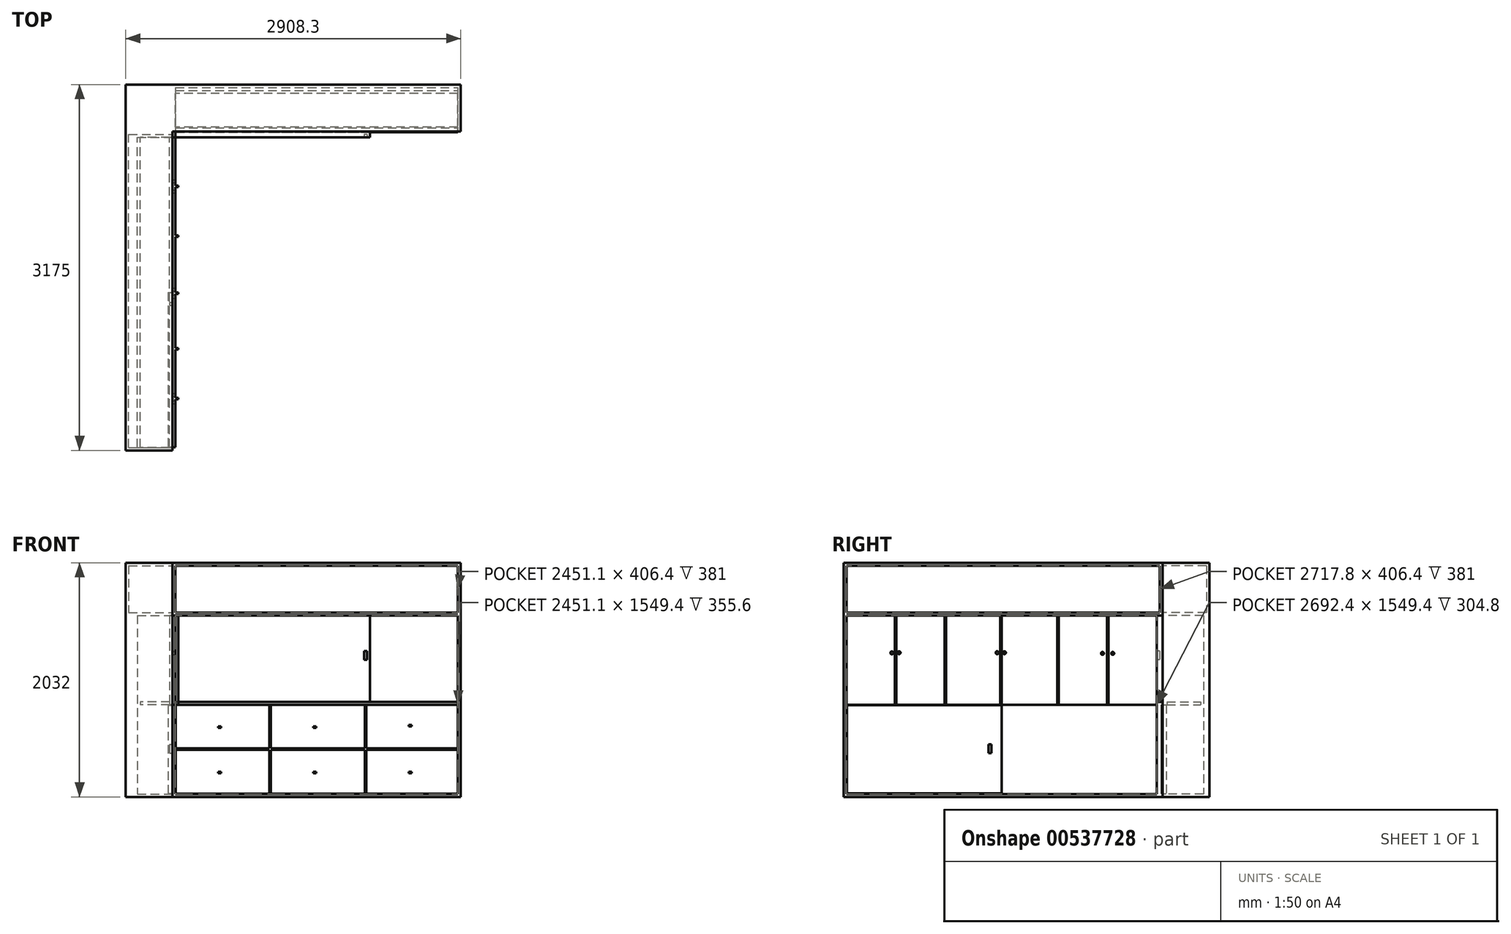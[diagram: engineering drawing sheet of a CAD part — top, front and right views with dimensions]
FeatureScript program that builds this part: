
annotation { "Feature Type Name" : "Feature", "Feature Type Description" : "" }
export const myFeature = defineFeature(function(context is Context, id is Id, definition is map)
    precondition{}
    {
        {
            var Q0;
            Q0=qCreatedBy(makeId("Top.planeOp"),FACE);
            var sketch = newSketch(context, id + "F0", { "sketchPlane" : qUnion([Q0])});
            skLineSegment(sketch, "E0", {"start": v(0, 0) * mm, "end": v(0, 3175) * mm});
            skLineSegment(sketch, "E1", {"start": v(0, 3175) * mm, "end": v(2908.3, 3175) * mm});
            skLineSegment(sketch, "E2", {"start": v(2908.3, 3175) * mm, "end": v(2908.3, 2768.6) * mm});
            skLineSegment(sketch, "E3", {"start": v(0, 0) * mm, "end": v(406.4, 0) * mm});
            skLineSegment(sketch, "E4", {"start": v(406.4, 0) * mm, "end": v(406.4, 2768.6) * mm});
            skLineSegment(sketch, "E5", {"start": v(406.4, 2768.6) * mm, "end": v(2908.3, 2768.6) * mm});
            skSolve(sketch);
        }
        {
            var Q0;
            Q0 = qSketchRegion(id + "F0", true);
            extrude(context, id + "F1", {"entities" : qUnion([Q0]), "depth" : 2032 * mm, "offsetDistance" : 25.4 * mm});
        }
        {
            var Q0;
            Q0=makeQuery(id+"F1.opExtrude","SWEPT_FACE",FACE,{"disambiguationData":[OSD([sQuery(id+"F0.wireOp",EDGE,"E4")])]});
            cPlane(context, id + "F2", {"entities" : qUnion([Q0]), "cplaneType" : CPlaneType.OFFSET, "offset" : 25.4 * mm, "width" : 152.4 * mm, "height" : 152.4 * mm});
        }
        {
            var Q0;
            Q0=makeQuery(id+"F1.opExtrude","SWEPT_FACE",FACE,{"disambiguationData":[OSD([sQuery(id+"F0.wireOp",EDGE,"E4")])]});
            var sketch = newSketch(context, id + "F3", { "sketchPlane" : qUnion([Q0])});
            skLineSegment(sketch, "E6.bottom", {"start": v(25.4, 2006.6) * mm, "end": v(2743.2, 2006.6) * mm});
            skLineSegment(sketch, "E6.top", {"start": v(25.4, 1600.2) * mm, "end": v(2743.2, 1600.2) * mm});
            skLineSegment(sketch, "E6.left", {"start": v(25.4, 2006.6) * mm, "end": v(25.4, 1600.2) * mm});
            skLineSegment(sketch, "E6.right", {"start": v(2743.2, 2006.6) * mm, "end": v(2743.2, 1600.2) * mm});
            skSolve(sketch);
        }
        {
            var Q0;
            Q0=makeQuery(id+"F3.imprint","IMPRINT",FACE,{"disambiguationData":[TD([[makeQuery(id+"F3.imprint","IMPRINT",EDGE,{"derivedFrom":sQuery(id+"F3.wireOp",EDGE,"E6.bottom")}),-1.0]])]});
            extrude(context, id + "F4", {"entities" : qUnion([Q0]), "operationType" : NewBodyOperationType.REMOVE, "oppositeDirection" : true, "depth" : 381 * mm, "offsetDistance" : 25.4 * mm});
        }
        {
            var Q0;
            Q0=qCreatedBy(id+"F2.planeOp",FACE);
            var sketch = newSketch(context, id + "F5", { "sketchPlane" : qUnion([Q0])});
            skLineSegment(sketch, "E7.bottom", {"start": v(25.4, 1574.8) * mm, "end": v(2717.8, 1574.8) * mm});
            skLineSegment(sketch, "E7.top", {"start": v(25.4, 25.4) * mm, "end": v(2717.8, 25.4) * mm});
            skLineSegment(sketch, "E7.left", {"start": v(25.4, 1574.8) * mm, "end": v(25.4, 25.4) * mm});
            skLineSegment(sketch, "E7.right", {"start": v(2717.8, 1574.8) * mm, "end": v(2717.8, 25.4) * mm});
            skSolve(sketch);
        }
        {
            var Q0;
            Q0 = qSketchRegion(id + "F5", true);
            extrude(context, id + "F6", {"entities" : qUnion([Q0]), "operationType" : NewBodyOperationType.REMOVE, "oppositeDirection" : true, "depth" : 330.2 * mm, "offsetDistance" : 25.4 * mm});
        }
        {
            var Q0;
            Q0=makeQuery(id+"F1.opExtrude","SWEPT_FACE",FACE,{"disambiguationData":[OSD([sQuery(id+"F0.wireOp",EDGE,"E5")])]});
            cPlane(context, id + "F7", {"entities" : qUnion([Q0]), "cplaneType" : CPlaneType.OFFSET, "offset" : 25.4 * mm, "width" : 152.4 * mm, "height" : 152.4 * mm});
        }
        {
            var Q0;
            Q0=qCreatedBy(id+"F7.planeOp",FACE);
            var sketch = newSketch(context, id + "F8", { "sketchPlane" : qUnion([Q0])});
            skLineSegment(sketch, "E8.bottom", {"start": v(431.8, 2006.6) * mm, "end": v(2882.9, 2006.6) * mm});
            skLineSegment(sketch, "E8.top", {"start": v(431.8, 1600.2) * mm, "end": v(2882.9, 1600.2) * mm});
            skLineSegment(sketch, "E8.left", {"start": v(431.8, 2006.6) * mm, "end": v(431.8, 1600.2) * mm});
            skLineSegment(sketch, "E8.right", {"start": v(2882.9, 2006.6) * mm, "end": v(2882.9, 1600.2) * mm});
            skSolve(sketch);
        }
        {
            var Q0;
            Q0 = qSketchRegion(id + "F8", true);
            extrude(context, id + "F9", {"entities" : qUnion([Q0]), "operationType" : NewBodyOperationType.REMOVE, "oppositeDirection" : true, "depth" : 406.4 * mm, "offsetDistance" : 25.4 * mm});
        }
        {
            var Q0;
            Q0=makeQuery(id+"F6.boolean.opBoolean","COPY",FACE,{"derivedFrom":makeQuery(id+"F6.opExtrude","CAP_FACE",FACE,{"disambiguationData":[OSD([sQuery(id+"F5.wireOp",EDGE,"E7.bottom"),sQuery(id+"F5.wireOp",EDGE,"E7.top"),sQuery(id+"F5.wireOp",EDGE,"E7.left"),sQuery(id+"F5.wireOp",EDGE,"E7.right")])],"isStart":false})});
            cPlane(context, id + "F10", {"entities" : qUnion([Q0]), "cplaneType" : CPlaneType.OFFSET, "offset" : 25.4 * mm, "width" : 152.4 * mm, "height" : 152.4 * mm});
        }
        {
            var Q0;
            Q0=qCreatedBy(id+"F10.planeOp",FACE);
            var sketch = newSketch(context, id + "F11", { "sketchPlane" : qUnion([Q0])});
            skLineSegment(sketch, "E9.bottom", {"start": v(25.4, 825.5) * mm, "end": v(2717.8, 825.5) * mm});
            skLineSegment(sketch, "E9.top", {"start": v(25.4, 800.1) * mm, "end": v(2717.8, 800.1) * mm});
            skLineSegment(sketch, "E9.left", {"start": v(25.4, 825.5) * mm, "end": v(25.4, 800.1) * mm});
            skLineSegment(sketch, "E9.right", {"start": v(2717.8, 825.5) * mm, "end": v(2717.8, 800.1) * mm});
            skSolve(sketch);
        }
        {
            var Q0;
            Q0=makeQuery(id+"F11.imprint","IMPRINT",FACE,{"disambiguationData":[TD([[makeQuery(id+"F11.imprint","IMPRINT",EDGE,{"derivedFrom":sQuery(id+"F11.wireOp",EDGE,"E9.bottom")}),-1.0]])]});
            extrude(context, id + "F12", {"entities" : qUnion([Q0]), "depth" : 254 * mm, "offsetDistance" : 25.4 * mm});
        }
        {
            var Q0;
            Q0=makeQuery(id+"F12.opExtrude","CAP_FACE",FACE,{"disambiguationData":[OSD([sQuery(id+"F11.wireOp",EDGE,"E9.bottom"),sQuery(id+"F11.wireOp",EDGE,"E9.top"),sQuery(id+"F11.wireOp",EDGE,"E9.left"),sQuery(id+"F11.wireOp",EDGE,"E9.right")])],"isStart":false});
            cPlane(context, id + "F13", {"entities" : qUnion([Q0]), "cplaneType" : CPlaneType.OFFSET, "offset" : 25.4 * mm, "width" : 152.4 * mm, "height" : 152.4 * mm});
        }
        {
            var Q0;
            Q0=qCreatedBy(id+"F13.planeOp",FACE);
            var sketch = newSketch(context, id + "F14", { "sketchPlane" : qUnion([Q0])});
            skLineSegment(sketch, "E10.bottom", {"start": v(1371.6, 795.02) * mm, "end": v(29.21, 795.02) * mm});
            skLineSegment(sketch, "E10.top", {"start": v(1371.6, 29.2) * mm, "end": v(29.21, 29.2) * mm});
            skLineSegment(sketch, "E10.left", {"start": v(1371.6, 795.02) * mm, "end": v(1371.6, 29.2) * mm});
            skLineSegment(sketch, "E10.right", {"start": v(29.21, 795.02) * mm, "end": v(29.21, 29.2) * mm});
            skSolve(sketch);
        }
        {
            var Q0;
            Q0 = qSketchRegion(id + "F14", true);
            extrude(context, id + "F15", {"entities" : qUnion([Q0]), "operationType" : NewBodyOperationType.ADD, "oppositeDirection" : true, "depth" : 38.1 * mm, "offsetDistance" : 25.4 * mm});
        }
        {
            var Q0;
            Q0=makeQuery(id+"F1.opExtrude","SWEPT_FACE",FACE,{"disambiguationData":[OSD([sQuery(id+"F0.wireOp",EDGE,"E5")])]});
            cPlane(context, id + "F16", {"entities" : qUnion([Q0]), "cplaneType" : CPlaneType.OFFSET, "offset" : 25.4 * mm, "width" : 152.4 * mm, "height" : 152.4 * mm});
        }
        {
            var Q0;
            Q0=makeQuery(id+"F1.opExtrude","SWEPT_FACE",FACE,{"disambiguationData":[OSD([sQuery(id+"F0.wireOp",EDGE,"E5")])]});
            var sketch = newSketch(context, id + "F17", { "sketchPlane" : qUnion([Q0])});
            skLineSegment(sketch, "E11.bottom", {"start": v(431.8, 1574.8) * mm, "end": v(2882.9, 1574.8) * mm});
            skLineSegment(sketch, "E11.top", {"start": v(431.8, 25.4) * mm, "end": v(2882.9, 25.4) * mm});
            skLineSegment(sketch, "E11.left", {"start": v(431.8, 1574.8) * mm, "end": v(431.8, 25.4) * mm});
            skLineSegment(sketch, "E11.right", {"start": v(2882.9, 1574.8) * mm, "end": v(2882.9, 25.4) * mm});
            skSolve(sketch);
        }
        {
            var Q0;
            Q0 = qSketchRegion(id + "F17", true);
            extrude(context, id + "F18", {"entities" : qUnion([Q0]), "operationType" : NewBodyOperationType.REMOVE, "oppositeDirection" : true, "depth" : 355.6 * mm, "offsetDistance" : 25.4 * mm});
        }
        {
            var Q0;
            Q0=makeQuery(id+"F18.boolean.opBoolean","COPY",FACE,{"derivedFrom":makeQuery(id+"F18.opExtrude","CAP_FACE",FACE,{"disambiguationData":[OSD([sQuery(id+"F17.wireOp",EDGE,"E11.bottom"),sQuery(id+"F17.wireOp",EDGE,"E11.top"),sQuery(id+"F17.wireOp",EDGE,"E11.left"),sQuery(id+"F17.wireOp",EDGE,"E11.right")])],"isStart":false})});
            cPlane(context, id + "F19", {"entities" : qUnion([Q0]), "cplaneType" : CPlaneType.OFFSET, "offset" : 25.4 * mm, "width" : 152.4 * mm, "height" : 152.4 * mm});
        }
        {
            var Q0;
            Q0=qCreatedBy(id+"F19.planeOp",FACE);
            var sketch = newSketch(context, id + "F20", { "sketchPlane" : qUnion([Q0])});
            skLineSegment(sketch, "E12.bottom", {"start": v(2882.9, 825.5) * mm, "end": v(431.8, 825.5) * mm});
            skLineSegment(sketch, "E12.top", {"start": v(2882.9, 800.1) * mm, "end": v(431.8, 800.1) * mm});
            skLineSegment(sketch, "E12.left", {"start": v(2882.9, 825.5) * mm, "end": v(2882.9, 800.1) * mm});
            skLineSegment(sketch, "E12.right", {"start": v(431.8, 825.5) * mm, "end": v(431.8, 800.1) * mm});
            skSolve(sketch);
        }
        {
            var Q0;
            Q0 = qSketchRegion(id + "F20", true);
            extrude(context, id + "F21", {"entities" : qUnion([Q0]), "operationType" : NewBodyOperationType.ADD, "depth" : 292.1 * mm, "offsetDistance" : 25.4 * mm});
        }
        {
            var Q0;
            Q0=makeQuery(id+"F21.opExtrude","CAP_FACE",FACE,{"disambiguationData":[OSD([sQuery(id+"F20.wireOp",EDGE,"E12.bottom"),sQuery(id+"F20.wireOp",EDGE,"E12.top"),sQuery(id+"F20.wireOp",EDGE,"E12.left"),sQuery(id+"F20.wireOp",EDGE,"E12.right")])],"isStart":false});
            cPlane(context, id + "F22", {"entities" : qUnion([Q0]), "cplaneType" : CPlaneType.OFFSET, "offset" : 25.4 * mm, "width" : 152.4 * mm, "height" : 152.4 * mm});
        }
        {
            var Q0;
            Q0=qCreatedBy(id+"F22.planeOp",FACE);
            var sketch = newSketch(context, id + "F23", { "sketchPlane" : qUnion([Q0])});
            skLineSegment(sketch, "E13.bottom", {"start": v(434.34, 797.56) * mm, "end": v(2880.36, 797.56) * mm});
            skLineSegment(sketch, "E13.top", {"start": v(434.34, 27.94) * mm, "end": v(2880.36, 27.94) * mm});
            skLineSegment(sketch, "E13.left", {"start": v(434.34, 797.56) * mm, "end": v(434.34, 27.94) * mm});
            skLineSegment(sketch, "E13.right", {"start": v(2880.36, 797.56) * mm, "end": v(2880.36, 27.94) * mm});
            skSolve(sketch);
        }
        {
            var Q0;
            Q0 = qSketchRegion(id + "F23", true);
            extrude(context, id + "F24", {"entities" : qUnion([Q0]), "depth" : 19.05 * mm, "offsetDistance" : 25.4 * mm, "hasSecondDirection" : true, "secondDirectionOppositeDirection" : true, "secondDirectionDepth" : 19.05 * mm});
        }
        {
            var Q0;
            Q0=qCreatedBy(id+"F16.planeOp",FACE);
            var sketch = newSketch(context, id + "F25", { "sketchPlane" : qUnion([Q0])});
            skLineSegment(sketch, "E14.bottom", {"start": v(436.88, 408.94) * mm, "end": v(2877.82, 408.94) * mm});
            skLineSegment(sketch, "E14.top", {"start": v(436.88, 421.64) * mm, "end": v(2877.82, 421.64) * mm});
            skLineSegment(sketch, "E14.left", {"start": v(436.88, 408.94) * mm, "end": v(436.88, 421.64) * mm});
            skLineSegment(sketch, "E14.right", {"start": v(2877.82, 408.94) * mm, "end": v(2877.82, 421.64) * mm});
            skLineSegment(sketch, "E15.bottom", {"start": v(1247.9, 421.64) * mm, "end": v(1260.6, 421.64) * mm});
            skLineSegment(sketch, "E15.top", {"start": v(1247.9, 797.3) * mm, "end": v(1260.6, 797.3) * mm});
            skLineSegment(sketch, "E15.left", {"start": v(1260.6, 421.64) * mm, "end": v(1260.6, 797.3) * mm});
            skLineSegment(sketch, "E15.right", {"start": v(1247.9, 421.64) * mm, "end": v(1247.9, 797.3) * mm});
            skLineSegment(sketch, "E16.bottom", {"start": v(1247.9, 408.94) * mm, "end": v(1260.6, 408.94) * mm});
            skLineSegment(sketch, "E16.top", {"start": v(1247.9, 28.2) * mm, "end": v(1260.6, 28.2) * mm});
            skLineSegment(sketch, "E16.left", {"start": v(1247.9, 408.94) * mm, "end": v(1247.9, 28.2) * mm});
            skLineSegment(sketch, "E16.right", {"start": v(1260.6, 408.94) * mm, "end": v(1260.6, 28.2) * mm});
            skLineSegment(sketch, "E17.bottom", {"start": v(2074.16, 421.64) * mm, "end": v(2086.86, 421.64) * mm});
            skLineSegment(sketch, "E17.top", {"start": v(2074.16, 797.3) * mm, "end": v(2086.86, 797.3) * mm});
            skLineSegment(sketch, "E17.left", {"start": v(2074.16, 421.64) * mm, "end": v(2074.16, 797.3) * mm});
            skLineSegment(sketch, "E17.right", {"start": v(2086.86, 421.64) * mm, "end": v(2086.86, 797.3) * mm});
            skLineSegment(sketch, "E18.bottom", {"start": v(2074.16, 408.94) * mm, "end": v(2086.86, 408.94) * mm});
            skLineSegment(sketch, "E18.top", {"start": v(2074.16, 33.02) * mm, "end": v(2086.86, 33.02) * mm});
            skLineSegment(sketch, "E18.left", {"start": v(2074.16, 408.94) * mm, "end": v(2074.16, 33.02) * mm});
            skLineSegment(sketch, "E18.right", {"start": v(2086.86, 408.94) * mm, "end": v(2086.86, 33.02) * mm});
            skSolve(sketch);
        }
        {
            var Q0;
            Q0 = qSketchRegion(id + "F25", true);
            extrude(context, id + "F26", {"entities" : qUnion([Q0]), "operationType" : NewBodyOperationType.REMOVE, "oppositeDirection" : true, "depth" : 25.4 * mm, "offsetDistance" : 25.4 * mm});
        }
        {
            var Q0;
            Q0=qCreatedBy(id+"F16.planeOp",FACE);
            var sketch = newSketch(context, id + "F27", { "sketchPlane" : qUnion([Q0])});
            skLineSegment(sketch, "E19.bottom", {"start": v(802.64, 612.14) * mm, "end": v(828.04, 612.14) * mm});
            skLineSegment(sketch, "E19.top", {"start": v(802.64, 599.44) * mm, "end": v(828.04, 599.44) * mm});
            skLineSegment(sketch, "E19.left", {"start": v(802.64, 612.14) * mm, "end": v(802.64, 599.44) * mm});
            skLineSegment(sketch, "E19.right", {"start": v(828.04, 612.14) * mm, "end": v(828.04, 599.44) * mm});
            skLineSegment(sketch, "E20.bottom", {"start": v(802.64, 218.44) * mm, "end": v(828.04, 218.44) * mm});
            skLineSegment(sketch, "E20.top", {"start": v(802.64, 205.74) * mm, "end": v(828.04, 205.74) * mm});
            skLineSegment(sketch, "E20.left", {"start": v(802.64, 218.44) * mm, "end": v(802.64, 205.74) * mm});
            skLineSegment(sketch, "E20.right", {"start": v(828.04, 218.44) * mm, "end": v(828.04, 205.74) * mm});
            skLineSegment(sketch, "E21.bottom", {"start": v(1628.9, 612.14) * mm, "end": v(1654.3, 612.14) * mm});
            skLineSegment(sketch, "E21.top", {"start": v(1628.9, 599.44) * mm, "end": v(1654.3, 599.44) * mm});
            skLineSegment(sketch, "E21.left", {"start": v(1628.9, 612.14) * mm, "end": v(1628.9, 599.44) * mm});
            skLineSegment(sketch, "E21.right", {"start": v(1654.3, 612.14) * mm, "end": v(1654.3, 599.44) * mm});
            skLineSegment(sketch, "E22.bottom", {"start": v(1628.9, 218.44) * mm, "end": v(1654.3, 218.44) * mm});
            skLineSegment(sketch, "E22.top", {"start": v(1628.9, 205.74) * mm, "end": v(1654.3, 205.74) * mm});
            skLineSegment(sketch, "E22.left", {"start": v(1628.9, 218.44) * mm, "end": v(1628.9, 205.74) * mm});
            skLineSegment(sketch, "E22.right", {"start": v(1654.3, 218.44) * mm, "end": v(1654.3, 205.74) * mm});
            skLineSegment(sketch, "E23.bottom", {"start": v(2455.16, 624.84) * mm, "end": v(2480.56, 624.84) * mm});
            skLineSegment(sketch, "E23.top", {"start": v(2455.16, 612.14) * mm, "end": v(2480.56, 612.14) * mm});
            skLineSegment(sketch, "E23.left", {"start": v(2455.16, 624.84) * mm, "end": v(2455.16, 612.14) * mm});
            skLineSegment(sketch, "E23.right", {"start": v(2480.56, 624.84) * mm, "end": v(2480.56, 612.14) * mm});
            skLineSegment(sketch, "E24.bottom", {"start": v(2455.16, 218.44) * mm, "end": v(2480.56, 218.44) * mm});
            skLineSegment(sketch, "E24.top", {"start": v(2455.16, 205.74) * mm, "end": v(2480.56, 205.74) * mm});
            skLineSegment(sketch, "E24.left", {"start": v(2455.16, 218.44) * mm, "end": v(2455.16, 205.74) * mm});
            skLineSegment(sketch, "E24.right", {"start": v(2480.56, 218.44) * mm, "end": v(2480.56, 205.74) * mm});
            skSolve(sketch);
        }
        {
            var Q0;
            Q0 = qSketchRegion(id + "F27", true);
            extrude(context, id + "F28", {"entities" : qUnion([Q0]), "operationType" : NewBodyOperationType.REMOVE, "oppositeDirection" : true, "depth" : 25.4 * mm, "offsetDistance" : 25.4 * mm});
        }
        {
            var Q0;
            Q0=qCreatedBy(id+"F16.planeOp",FACE);
            var sketch = newSketch(context, id + "F29", { "sketchPlane" : qUnion([Q0])});
            skLineSegment(sketch, "E25.bottom", {"start": v(432.05, 1574.55) * mm, "end": v(2120.9, 1574.55) * mm});
            skLineSegment(sketch, "E25.top", {"start": v(432.05, 825.75) * mm, "end": v(2120.9, 825.75) * mm});
            skLineSegment(sketch, "E25.left", {"start": v(432.05, 1574.55) * mm, "end": v(432.05, 825.75) * mm});
            skLineSegment(sketch, "E25.right", {"start": v(2120.9, 1574.55) * mm, "end": v(2120.9, 825.75) * mm});
            skSolve(sketch);
        }
        {
            var Q0;
            Q0 = qSketchRegion(id + "F29", true);
            extrude(context, id + "F30", {"entities" : qUnion([Q0]), "depth" : 25.4 * mm, "offsetDistance" : 25.4 * mm, "hasSecondDirection" : true, "secondDirectionOppositeDirection" : true, "secondDirectionDepth" : 25.4 * mm});
        }
        {
            var Q0;
            Q0=makeQuery(id+"F30.opExtrude","CAP_FACE",FACE,{"disambiguationData":[OSD([sQuery(id+"F29.wireOp",EDGE,"E25.bottom"),sQuery(id+"F29.wireOp",EDGE,"E25.top"),sQuery(id+"F29.wireOp",EDGE,"E25.left"),sQuery(id+"F29.wireOp",EDGE,"E25.right")])],"isStart":false});
            var sketch = newSketch(context, id + "F31", { "sketchPlane" : qUnion([Q0])});
            skLineSegment(sketch, "E26.bottom", {"start": v(2095.5, 1266.45) * mm, "end": v(2070.1, 1266.45) * mm});
            skLineSegment(sketch, "E26.top", {"start": v(2095.5, 1190.25) * mm, "end": v(2070.1, 1190.25) * mm});
            skLineSegment(sketch, "E26.left", {"start": v(2095.5, 1266.45) * mm, "end": v(2095.5, 1190.25) * mm});
            skLineSegment(sketch, "E26.right", {"start": v(2070.1, 1266.45) * mm, "end": v(2070.1, 1190.25) * mm});
            skSolve(sketch);
        }
        {
            var Q0;
            Q0 = qSketchRegion(id + "F31", true);
            extrude(context, id + "F32", {"entities" : qUnion([Q0]), "operationType" : NewBodyOperationType.REMOVE, "oppositeDirection" : true, "depth" : 25.4 * mm, "offsetDistance" : 25.4 * mm});
        }
        {
            var Q0;
            Q0=makeQuery(id+"F14.imprint","IMPRINT",FACE,{"disambiguationData":[TD([[makeQuery(id+"F14.imprint","IMPRINT",EDGE,{"derivedFrom":sQuery(id+"F14.wireOp",EDGE,"E10.bottom")}),1.0]])]});
            var sketch = newSketch(context, id + "F33", { "sketchPlane" : qUnion([Q0])});
            skLineSegment(sketch, "E27.bottom", {"start": v(1283.1, 455.55) * mm, "end": v(1257.7, 455.55) * mm});
            skLineSegment(sketch, "E27.top", {"start": v(1283.1, 379.35) * mm, "end": v(1257.7, 379.35) * mm});
            skLineSegment(sketch, "E27.left", {"start": v(1283.1, 455.55) * mm, "end": v(1283.1, 379.35) * mm});
            skLineSegment(sketch, "E27.right", {"start": v(1257.7, 455.55) * mm, "end": v(1257.7, 379.35) * mm});
            skSolve(sketch);
        }
        {
            var Q0;
            Q0 = qSketchRegion(id + "F33", true);
            extrude(context, id + "F34", {"entities" : qUnion([Q0]), "operationType" : NewBodyOperationType.REMOVE, "oppositeDirection" : true, "depth" : 25.4 * mm, "offsetDistance" : 25.4 * mm});
        }
        {
            var Q0;
            Q0=qCreatedBy(id+"F13.planeOp",FACE);
            var sketch = newSketch(context, id + "F35", { "sketchPlane" : qUnion([Q0])});
            skLineSegment(sketch, "E28.bottom", {"start": v(25.65, 1574.55) * mm, "end": v(2717.55, 1574.55) * mm});
            skLineSegment(sketch, "E28.top", {"start": v(25.65, 797.56) * mm, "end": v(2717.55, 797.56) * mm});
            skLineSegment(sketch, "E28.left", {"start": v(25.65, 1574.55) * mm, "end": v(25.65, 797.56) * mm});
            skLineSegment(sketch, "E28.right", {"start": v(2717.55, 1574.55) * mm, "end": v(2717.55, 797.56) * mm});
            skSolve(sketch);
        }
        {
            var Q0;
            Q0 = qSketchRegion(id + "F35", true);
            extrude(context, id + "F36", {"entities" : qUnion([Q0]), "operationType" : NewBodyOperationType.ADD, "depth" : 25.4 * mm, "offsetDistance" : 25.4 * mm, "hasSecondDirection" : true, "secondDirectionOppositeDirection" : true, "secondDirectionDepth" : 25.4 * mm});
        }
        {
            var Q0;
            Q0=makeQuery(id+"F36.opExtrude","CAP_FACE",FACE,{"disambiguationData":[OSD([sQuery(id+"F35.wireOp",EDGE,"E28.bottom"),sQuery(id+"F35.wireOp",EDGE,"E28.top"),sQuery(id+"F35.wireOp",EDGE,"E28.left"),sQuery(id+"F35.wireOp",EDGE,"E28.right")])],"isStart":false});
            var sketch = newSketch(context, id + "F37", { "sketchPlane" : qUnion([Q0])});
            skLineSegment(sketch, "E29.bottom", {"start": v(444.5, 1574.55) * mm, "end": v(457.2, 1574.55) * mm});
            skLineSegment(sketch, "E29.top", {"start": v(444.5, 797.56) * mm, "end": v(457.2, 797.56) * mm});
            skLineSegment(sketch, "E29.left", {"start": v(444.5, 1574.55) * mm, "end": v(444.5, 797.56) * mm});
            skLineSegment(sketch, "E29.right", {"start": v(457.2, 1574.55) * mm, "end": v(457.2, 797.56) * mm});
            skLineSegment(sketch, "E30.bottom", {"start": v(876.3, 1574.55) * mm, "end": v(889, 1574.55) * mm});
            skLineSegment(sketch, "E30.top", {"start": v(876.3, 797.56) * mm, "end": v(889, 797.56) * mm});
            skLineSegment(sketch, "E30.left", {"start": v(876.3, 1574.55) * mm, "end": v(876.3, 797.56) * mm});
            skLineSegment(sketch, "E30.right", {"start": v(889, 1574.55) * mm, "end": v(889, 797.56) * mm});
            skLineSegment(sketch, "E31.bottom", {"start": v(2298.7, 1574.55) * mm, "end": v(2286, 1574.55) * mm});
            skLineSegment(sketch, "E31.top", {"start": v(2298.7, 797.56) * mm, "end": v(2286, 797.56) * mm});
            skLineSegment(sketch, "E31.left", {"start": v(2298.7, 1574.55) * mm, "end": v(2298.7, 797.56) * mm});
            skLineSegment(sketch, "E31.right", {"start": v(2286, 1574.55) * mm, "end": v(2286, 797.56) * mm});
            skLineSegment(sketch, "E32.bottom", {"start": v(1866.9, 1574.55) * mm, "end": v(1854.2, 1574.55) * mm});
            skLineSegment(sketch, "E32.top", {"start": v(1866.9, 797.56) * mm, "end": v(1854.2, 797.56) * mm});
            skLineSegment(sketch, "E32.left", {"start": v(1866.9, 1574.55) * mm, "end": v(1866.9, 797.56) * mm});
            skLineSegment(sketch, "E32.right", {"start": v(1854.2, 1574.55) * mm, "end": v(1854.2, 797.56) * mm});
            skLineSegment(sketch, "E33.bottom", {"start": v(1358.9, 1574.55) * mm, "end": v(1371.6, 1574.55) * mm});
            skLineSegment(sketch, "E33.top", {"start": v(1358.9, 797.56) * mm, "end": v(1371.6, 797.56) * mm});
            skLineSegment(sketch, "E33.left", {"start": v(1358.9, 1574.55) * mm, "end": v(1358.9, 797.56) * mm});
            skLineSegment(sketch, "E33.right", {"start": v(1371.6, 1574.55) * mm, "end": v(1371.6, 797.56) * mm});
            skSolve(sketch);
        }
        {
            var Q0;
            Q0 = qSketchRegion(id + "F37", true);
            extrude(context, id + "F38", {"entities" : qUnion([Q0]), "operationType" : NewBodyOperationType.ADD, "depth" : 25.4 * mm, "offsetDistance" : 25.4 * mm});
        }
        {
            var Q0;
            {var subQ0=sQuery(id+"F35.wireOp",EDGE,"E28.left");var subQ1=sQuery(id+"F35.wireOp",EDGE,"E28.top");var subQ2=sQuery(id+"F35.wireOp",EDGE,"E28.bottom");Q0=makeQuery(id+"F38.boolean.opBoolean","SPLIT",FACE,{"disambiguationData":[TD([makeQuery(id+"F36.opExtrude","SWEPT_FACE",FACE,{"disambiguationData":[OSD([subQ0])]})])],"derivedFrom":makeQuery(id+"F36.opExtrude","CAP_FACE",FACE,{"disambiguationData":[OSD([subQ2,subQ1,subQ0,sQuery(id+"F35.wireOp",EDGE,"E28.right")])],"isStart":false})});}
            var sketch = newSketch(context, id + "F39", { "sketchPlane" : qUnion([Q0])});
            skCircle(sketch, "E34", {"center": v(419.1, 1249.69) * mm, "radius": 12.7 * mm});
            skCircle(sketch, "E35", {"center": v(482.6, 1251.07) * mm, "radius": 12.7 * mm});
            skCircle(sketch, "E36", {"center": v(1333.5, 1251.07) * mm, "radius": 13.07 * mm});
            skCircle(sketch, "E37", {"center": v(1397, 1251.07) * mm, "radius": 12.7 * mm});
            skCircle(sketch, "E38", {"center": v(2247.9, 1245.05) * mm, "radius": 12.7 * mm});
            skCircle(sketch, "E39", {"center": v(2336.8, 1245.05) * mm, "radius": 12.7 * mm});
            skSolve(sketch);
        }
        {
            var Q0;
            Q0 = qSketchRegion(id + "F39", true);
            extrude(context, id + "F40", {"entities" : qUnion([Q0]), "operationType" : NewBodyOperationType.REMOVE, "oppositeDirection" : true, "depth" : 25.4 * mm, "offsetDistance" : 25.4 * mm});
        }
    });
